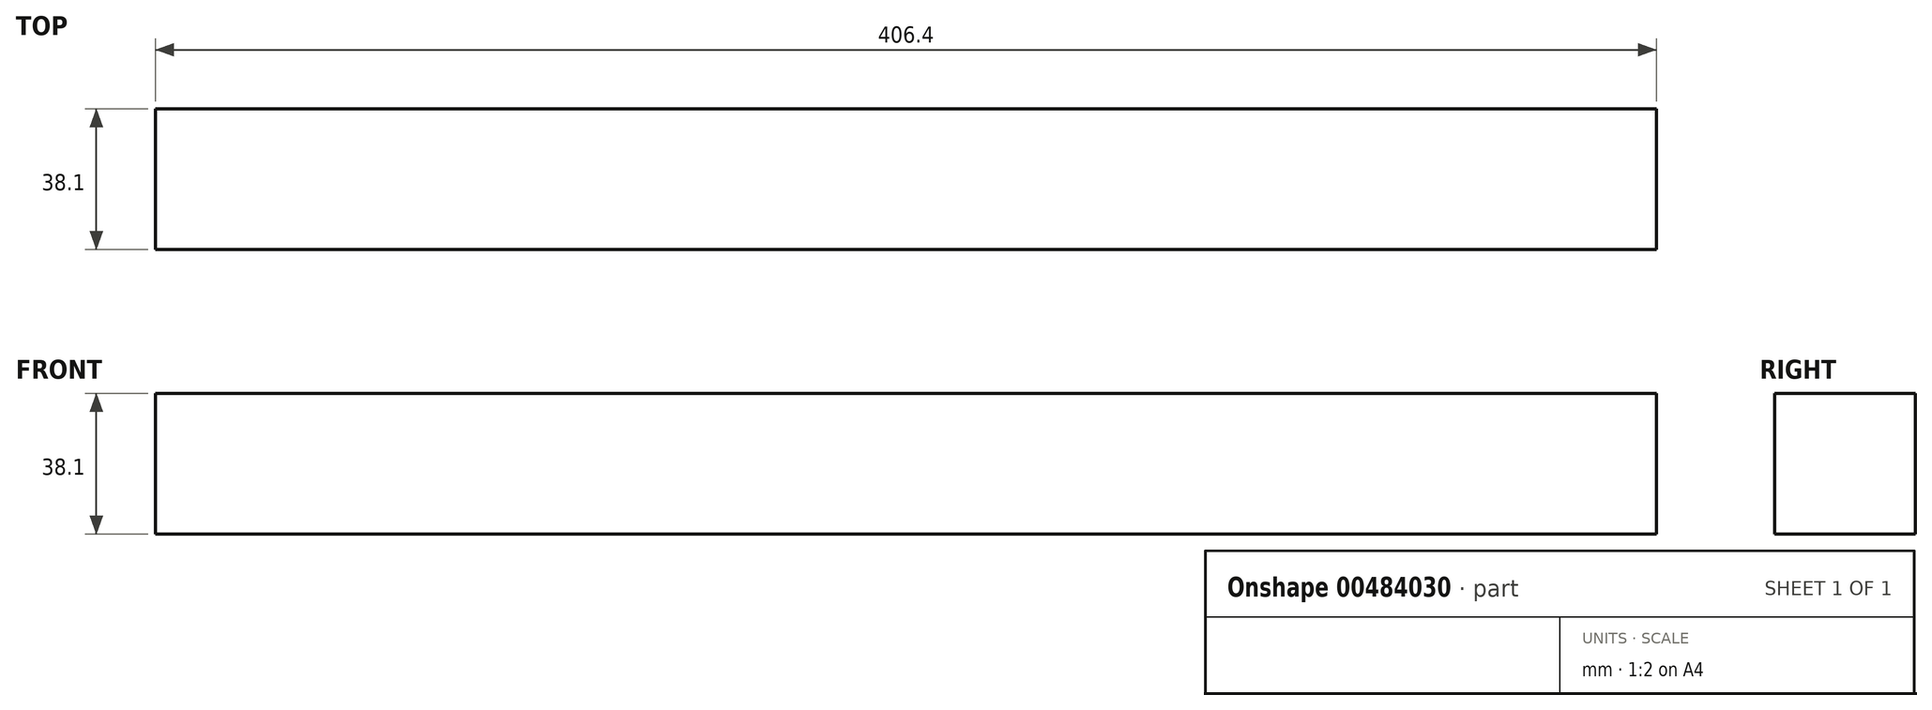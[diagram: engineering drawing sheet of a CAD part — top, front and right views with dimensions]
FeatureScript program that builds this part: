
annotation { "Feature Type Name" : "Feature", "Feature Type Description" : "" }
export const myFeature = defineFeature(function(context is Context, id is Id, definition is map)
    precondition{}
    {
        {
            var Q0;
            Q0=qCreatedBy(makeId("Right.planeOp"),FACE);
            var sketch = newSketch(context, id + "F0", { "sketchPlane" : qUnion([Q0])});
            skLineSegment(sketch, "E0.bottom", {"start": v(-19.05, 38.1) * mm, "end": v(19.05, 38.1) * mm});
            skLineSegment(sketch, "E0.top", {"start": v(-19.05, 0) * mm, "end": v(19.05, 0) * mm});
            skLineSegment(sketch, "E0.left", {"start": v(-19.05, 38.1) * mm, "end": v(-19.05, 0) * mm});
            skLineSegment(sketch, "E0.right", {"start": v(19.05, 38.1) * mm, "end": v(19.05, 0) * mm});
            skSolve(sketch);
        }
        {
            var Q0;
            Q0 = qSketchRegion(id + "F0", true);
            extrude(context, id + "F1", {"entities" : qUnion([Q0]), "endBound" : BoundingType.SYMMETRIC, "depth" : 406.4 * mm});
        }
    });
